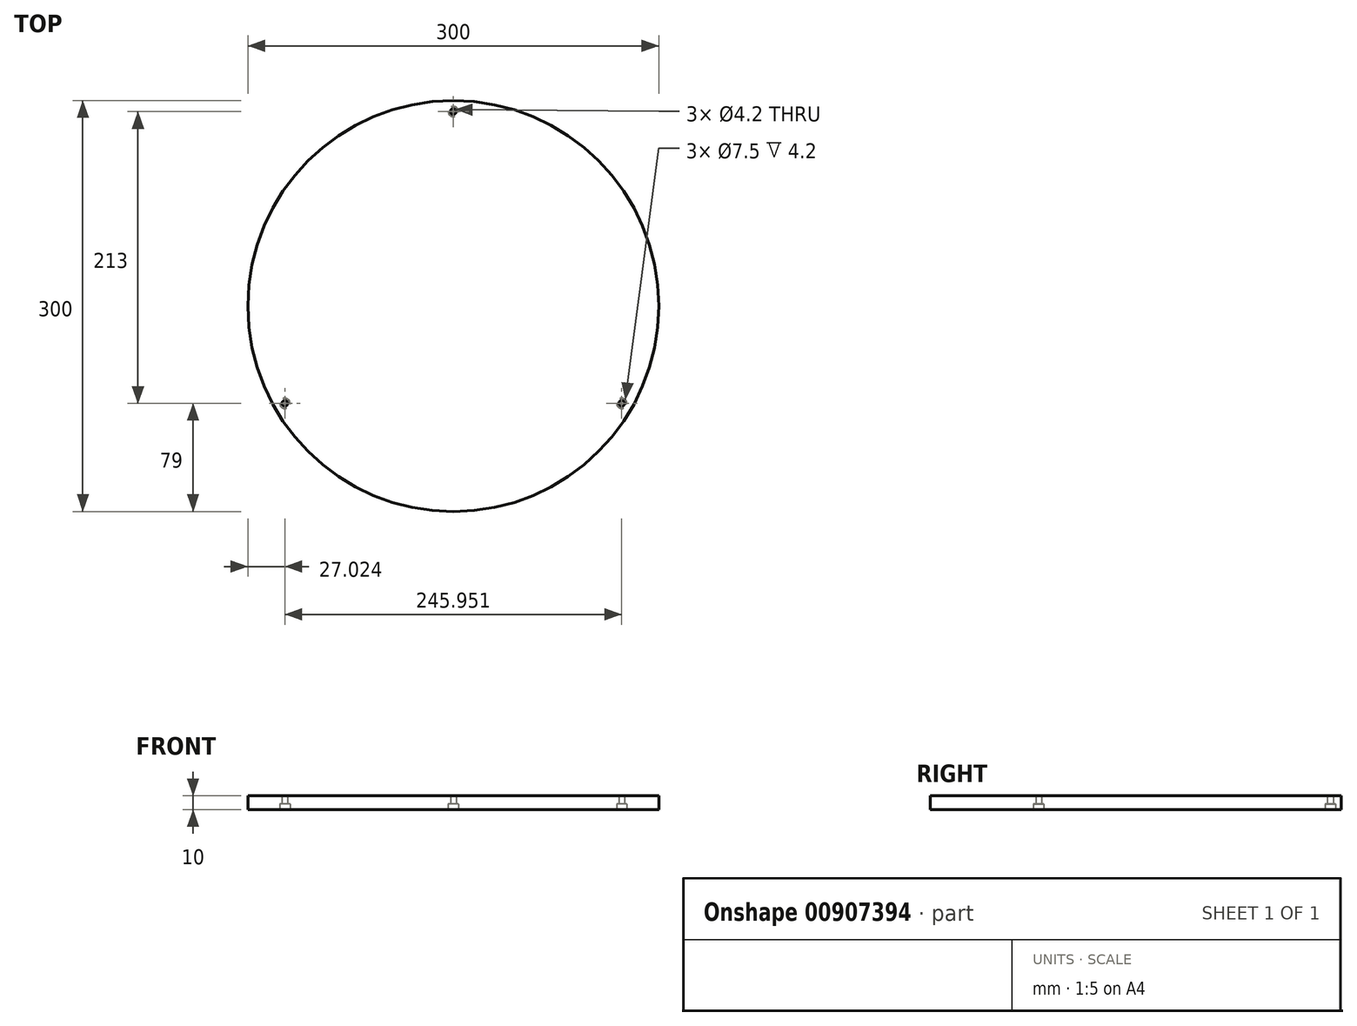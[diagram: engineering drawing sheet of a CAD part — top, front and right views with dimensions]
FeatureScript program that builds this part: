
annotation { "Feature Type Name" : "Feature", "Feature Type Description" : "" }
export const myFeature = defineFeature(function(context is Context, id is Id, definition is map)
    precondition{}
    {
        {
            var Q0;
            Q0=qCreatedBy(makeId("Top.planeOp"),FACE);
            var sketch = newSketch(context, id + "F0", { "sketchPlane" : qUnion([Q0])});
            skCircle(sketch, "E0", {"center": v(0, 0) * mm, "radius": 150 * mm});
            skCircle(sketch, "E1", {"center": v(0, 142) * mm, "radius": 2.1 * mm});
            skCircle(sketch, "E2", {"center": v(0, 142) * mm, "radius": 3.75 * mm});
            skCircle(sketch, "E3.1.0", {"center": v(122.98, -71) * mm, "radius": 2.1 * mm});
            skCircle(sketch, "E3.1.1", {"center": v(122.98, -71) * mm, "radius": 3.75 * mm});
            skCircle(sketch, "E3.2.0", {"center": v(-122.98, -71) * mm, "radius": 2.1 * mm});
            skCircle(sketch, "E3.2.1", {"center": v(-122.98, -71) * mm, "radius": 3.75 * mm});
            skLineSegment(sketch, "E3.anchor1", {"start": v(0, 0) * mm, "end": v(0, 142) * mm, "construction": true});
            skLineSegment(sketch, "E3.anchor2", {"start": v(0, 0) * mm, "end": v(-122.98, -71) * mm, "construction": true});
            skSolve(sketch);
        }
        {
            var Q0;
            Q0=makeQuery(id+"F0.imprint","IMPRINT",FACE,{"disambiguationData":[TD([[makeQuery(id+"F0.imprint","IMPRINT",EDGE,{"derivedFrom":sQuery(id+"F0.wireOp",EDGE,"E0")}),1.0]])]});
            var Q1;
            Q1=makeQuery(id+"F0.imprint","IMPRINT",FACE,{"disambiguationData":[TD([[makeQuery(id+"F0.imprint","IMPRINT",EDGE,{"derivedFrom":sQuery(id+"F0.wireOp",EDGE,"E1")}),-1.0]])]});
            var Q2;
            Q2=makeQuery(id+"F0.imprint","IMPRINT",FACE,{"disambiguationData":[TD([[makeQuery(id+"F0.imprint","IMPRINT",EDGE,{"derivedFrom":sQuery(id+"F0.wireOp",EDGE,"E3.1.0")}),-1.0]])]});
            var Q3;
            Q3=makeQuery(id+"F0.imprint","IMPRINT",FACE,{"disambiguationData":[TD([[makeQuery(id+"F0.imprint","IMPRINT",EDGE,{"derivedFrom":sQuery(id+"F0.wireOp",EDGE,"E3.2.0")}),-1.0]])]});
            extrude(context, id + "F1", {"entities" : qUnion([Q0, Q1, Q2, Q3]), "depth" : 10 * mm, "offsetDistance" : 25 * mm});
        }
        {
            var Q0;
            Q0=makeQuery(id+"F0.imprint","IMPRINT",FACE,{"disambiguationData":[TD([[makeQuery(id+"F0.imprint","IMPRINT",EDGE,{"derivedFrom":sQuery(id+"F0.wireOp",EDGE,"E3.2.0")}),-1.0]])]});
            var Q1;
            Q1=makeQuery(id+"F0.imprint","IMPRINT",FACE,{"disambiguationData":[TD([[makeQuery(id+"F0.imprint","IMPRINT",EDGE,{"derivedFrom":sQuery(id+"F0.wireOp",EDGE,"E3.1.0")}),-1.0]])]});
            var Q2;
            Q2=makeQuery(id+"F0.imprint","IMPRINT",FACE,{"disambiguationData":[TD([[makeQuery(id+"F0.imprint","IMPRINT",EDGE,{"derivedFrom":sQuery(id+"F0.wireOp",EDGE,"E1")}),-1.0]])]});
            extrude(context, id + "F2", {"entities" : qUnion([Q0, Q1, Q2]), "operationType" : NewBodyOperationType.REMOVE, "depth" : 4.2 * mm, "offsetDistance" : 25 * mm});
        }
    });
